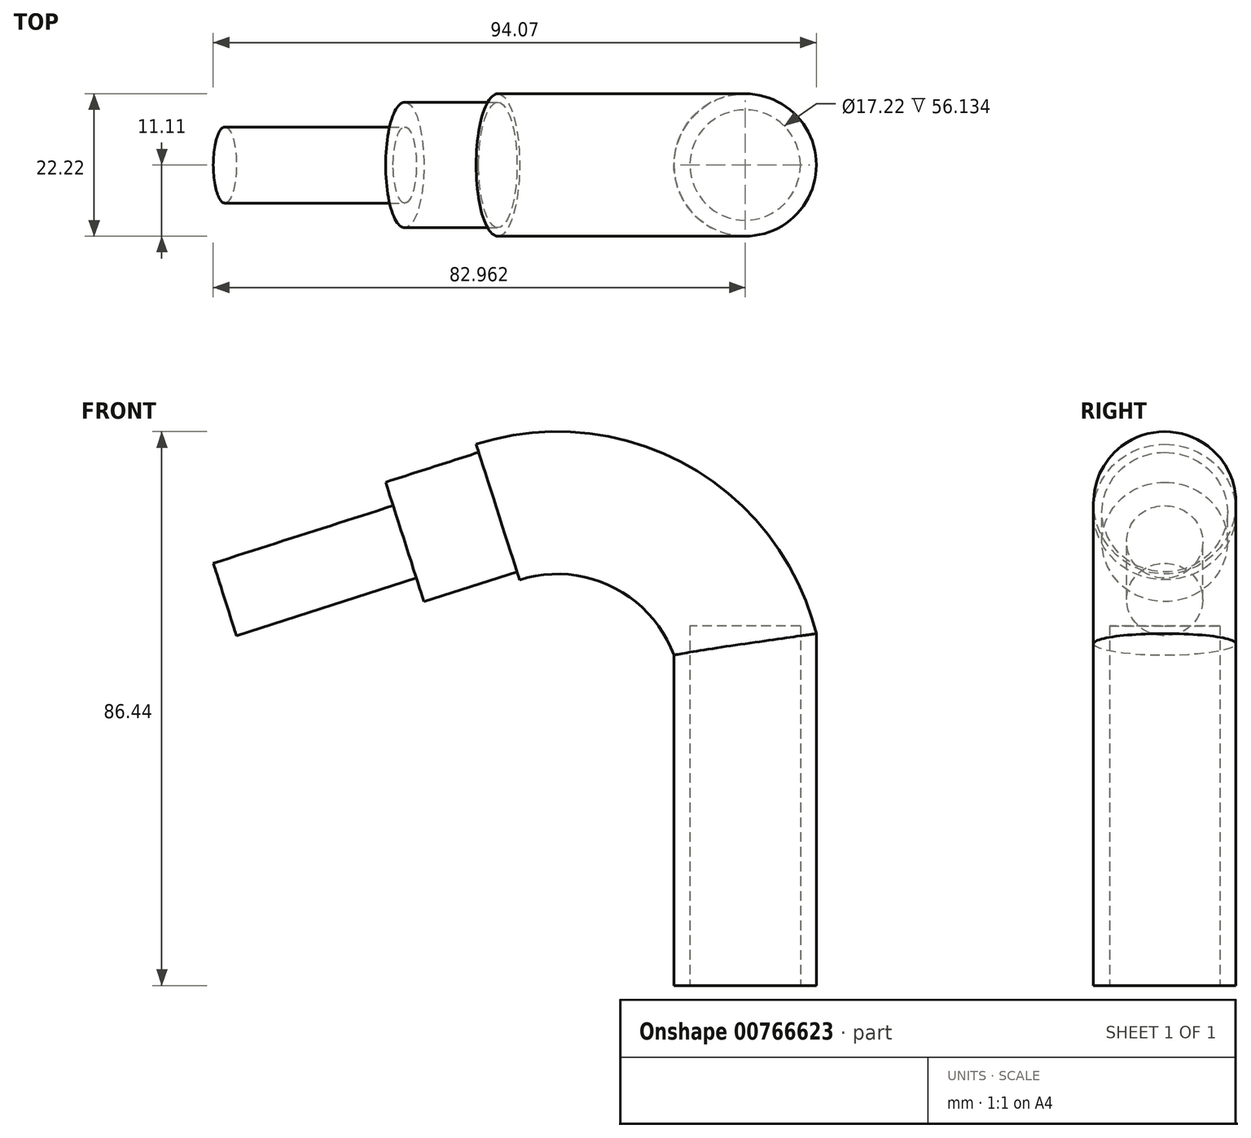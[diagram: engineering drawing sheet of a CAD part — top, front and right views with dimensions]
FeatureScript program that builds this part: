
annotation { "Feature Type Name" : "Feature", "Feature Type Description" : "" }
export const myFeature = defineFeature(function(context is Context, id is Id, definition is map)
    precondition{}
    {
        {
            var Q0;
            Q0=qCreatedBy(makeId("Front.planeOp"),FACE);
            var sketch = newSketch(context, id + "F0", { "sketchPlane" : qUnion([Q0])});
            skLineSegment(sketch, "E0", {"start": v(38.57, 0) * mm, "end": v(38.57, 53.34) * mm});
            skArc(sketch, "E1", {"start": v(38.57, 53.34) * mm, "mid": v(23.62, 71.76) * mm, "end": v(0, 73.88) * mm});
            skSolve(sketch);
        }
        {
            var Q0;
            Q0=qCreatedBy(makeId("Top.planeOp"),FACE);
            var sketch = newSketch(context, id + "F1", { "sketchPlane" : qUnion([Q0])});
            skCircle(sketch, "E2", {"center": v(38.57, 0) * mm, "radius": 11.11 * mm});
            skSolve(sketch);
        }
        {
            var Q0;
            Q0=makeQuery(id+"F1.imprint","IMPRINT",FACE,{"disambiguationData":[TD([[makeQuery(id+"F1.imprint","IMPRINT",EDGE,{"derivedFrom":sQuery(id+"F1.wireOp",EDGE,"E2")}),1.0]])]});
            var Q1;
            Q1=sQuery(id+"F0.wireOp",EDGE,"E0");
            var Q2;
            Q2=sQuery(id+"F0.wireOp",EDGE,"E1");
            sweep(context, id + "F2", {"profiles" : qUnion([Q0]), "path" : qUnion([Q1, Q2])});
        }
        {
            var Q0;
            Q0=qCreatedBy(makeId("Top.planeOp"),FACE);
            var sketch = newSketch(context, id + "F3", { "sketchPlane" : qUnion([Q0])});
            skCircle(sketch, "E3", {"center": v(38.57, 0) * mm, "radius": 8.61 * mm});
            skSolve(sketch);
        }
        {
            var Q0;
            Q0 = qSketchRegion(id + "F3", true);
            extrude(context, id + "F4", {"entities" : qUnion([Q0]), "operationType" : NewBodyOperationType.REMOVE, "depth" : 56.13 * mm, "offsetDistance" : 25.4 * mm});
        }
        {
            var Q0;
            Q0=makeQuery(id+"F2.opSweep","CAP_FACE",FACE,{"disambiguationData":[OSD([sQuery(id+"F0.wireOp",VERTEX,"E1.end"),sQuery(id+"F1.wireOp",EDGE,"E2")])],"isStart":false});
            var sketch = newSketch(context, id + "F5", { "sketchPlane" : qUnion([Q0])});
            skCircle(sketch, "E4", {"center": v(0, 70.36) * mm, "radius": 9.8 * mm});
            skSolve(sketch);
        }
        {
            var Q0;
            Q0=makeQuery(id+"F5.imprint","IMPRINT",FACE,{"disambiguationData":[TD([[makeQuery(id+"F5.imprint","IMPRINT",EDGE,{"derivedFrom":sQuery(id+"F5.wireOp",EDGE,"E4")}),1.0]])]});
            var Q1;
            Q1=sQuery(id+"F5.wireOp",EDGE,"E4");
            extrude(context, id + "F6", {"entities" : qUnion([Q0]), "operationType" : NewBodyOperationType.ADD, "surfaceEntities" : qUnion([Q1]), "depth" : 15.24 * mm, "offsetDistance" : 25.4 * mm});
        }
        {
            var Q0;
            Q0=makeQuery(id+"F6.opExtrude","CAP_FACE",FACE,{"disambiguationData":[OSD([sQuery(id+"F5.wireOp",EDGE,"E4")])],"isStart":false});
            var sketch = newSketch(context, id + "F7", { "sketchPlane" : qUnion([Q0])});
            skCircle(sketch, "E5", {"center": v(0, 70.36) * mm, "radius": 5.94 * mm});
            skSolve(sketch);
        }
        {
            var Q0;
            Q0 = qSketchRegion(id + "F7", true);
            extrude(context, id + "F8", {"entities" : qUnion([Q0]), "operationType" : NewBodyOperationType.ADD, "depth" : 29.46 * mm, "offsetDistance" : 25.4 * mm});
        }
    });
